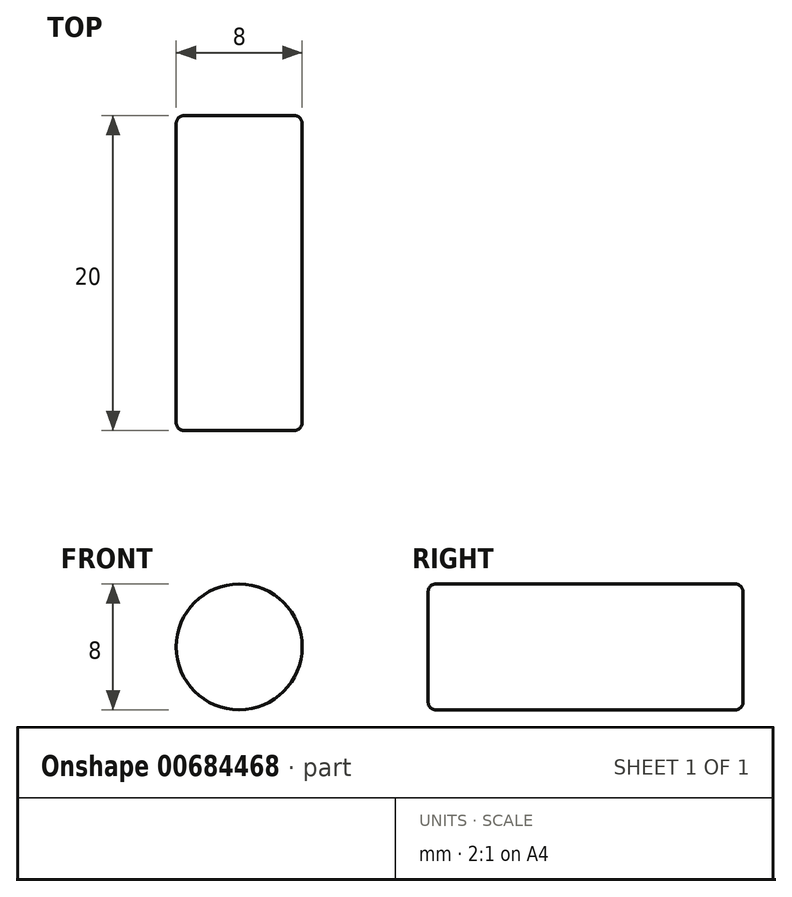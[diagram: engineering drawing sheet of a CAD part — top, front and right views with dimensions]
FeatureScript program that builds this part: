
annotation { "Feature Type Name" : "Feature", "Feature Type Description" : "" }
export const myFeature = defineFeature(function(context is Context, id is Id, definition is map)
    precondition{}
    {
        {
            var Q0;
            Q0=qCreatedBy(makeId("Front.planeOp"),FACE);
            var sketch = newSketch(context, id + "F0", { "sketchPlane" : qUnion([Q0])});
            skCircle(sketch, "E0", {"center": v(0, 0) * mm, "radius": 4 * mm});
            skSolve(sketch);
        }
        {
            var Q0;
            Q0=makeQuery(id+"F0.imprint","IMPRINT",FACE,{"disambiguationData":[TD([[makeQuery(id+"F0.imprint","IMPRINT",EDGE,{"derivedFrom":sQuery(id+"F0.wireOp",EDGE,"E0")}),1.0]])]});
            extrude(context, id + "F1", {"entities" : qUnion([Q0]), "depth" : 20 * mm, "offsetDistance" : 25 * mm});
        }
        {
            var Q0;
            Q0=makeQuery(id+"F1.opExtrude","CAP_EDGE",EDGE,{"disambiguationData":[OSD([sQuery(id+"F0.wireOp",EDGE,"E0")])],"isStart":false});
            var Q1;
            Q1=makeQuery(id+"F1.opExtrude","CAP_EDGE",EDGE,{"disambiguationData":[OSD([sQuery(id+"F0.wireOp",EDGE,"E0")])],"isStart":true});
            fillet(context, id + "F2", {"entities" : qUnion([Q0, Q1]), "radius" : .5 * mm, "tangentPropagation" : true, "allowEdgeOverflow" : false});
        }
    });
